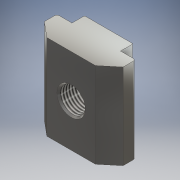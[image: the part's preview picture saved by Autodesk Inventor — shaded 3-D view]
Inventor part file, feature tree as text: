
AUTODESK INVENTOR PART (.ipt)
format: ipt  version: 2016 (Build 200138000, 138)  size: 155,136 bytes
history: native  units: mm
features: sketch x4, extrude x3, fillet x2, other x1, hole x1, chamfer x1, thread x1
ambient origin geometry x8: Origin, YZ Plane, XZ Plane, XY Plane, X Axis, Y Axis, Z Axis, Center Point
bodies: Body1 (feature_tree), Body2 (feature_tree), Body3 (feature_tree)
feature tree (13):
  other  "Твердое тело1"
  extrude  "Выдавливание1"  Depth=9.4mm
  extrude  "Выдавливание2"  Depth=4.5mm
  extrude  "Выдавливание3"  Depth=10.2mm TaperAngle=0.0deg
  hole  "Отверстие1"  [1 undecoded]
  chamfer  "Фаска1"  Distance=2.9mm
  fillet  "Сопряжение2"  Radius=5.8mm
  fillet  "Сопряжение3"  Radius=10.2mm
  thread  "Резьба2"
  sketch  "Эскиз1"
  sketch  "Эскиз3"
  sketch  "Эскиз5"
  sketch  "Эскиз6"
note: 1 required parameter value undecoded (feature->parameter linkage not recoverable at this tier; creation-order binding heuristic only, values carry confidence <= 0.55)
